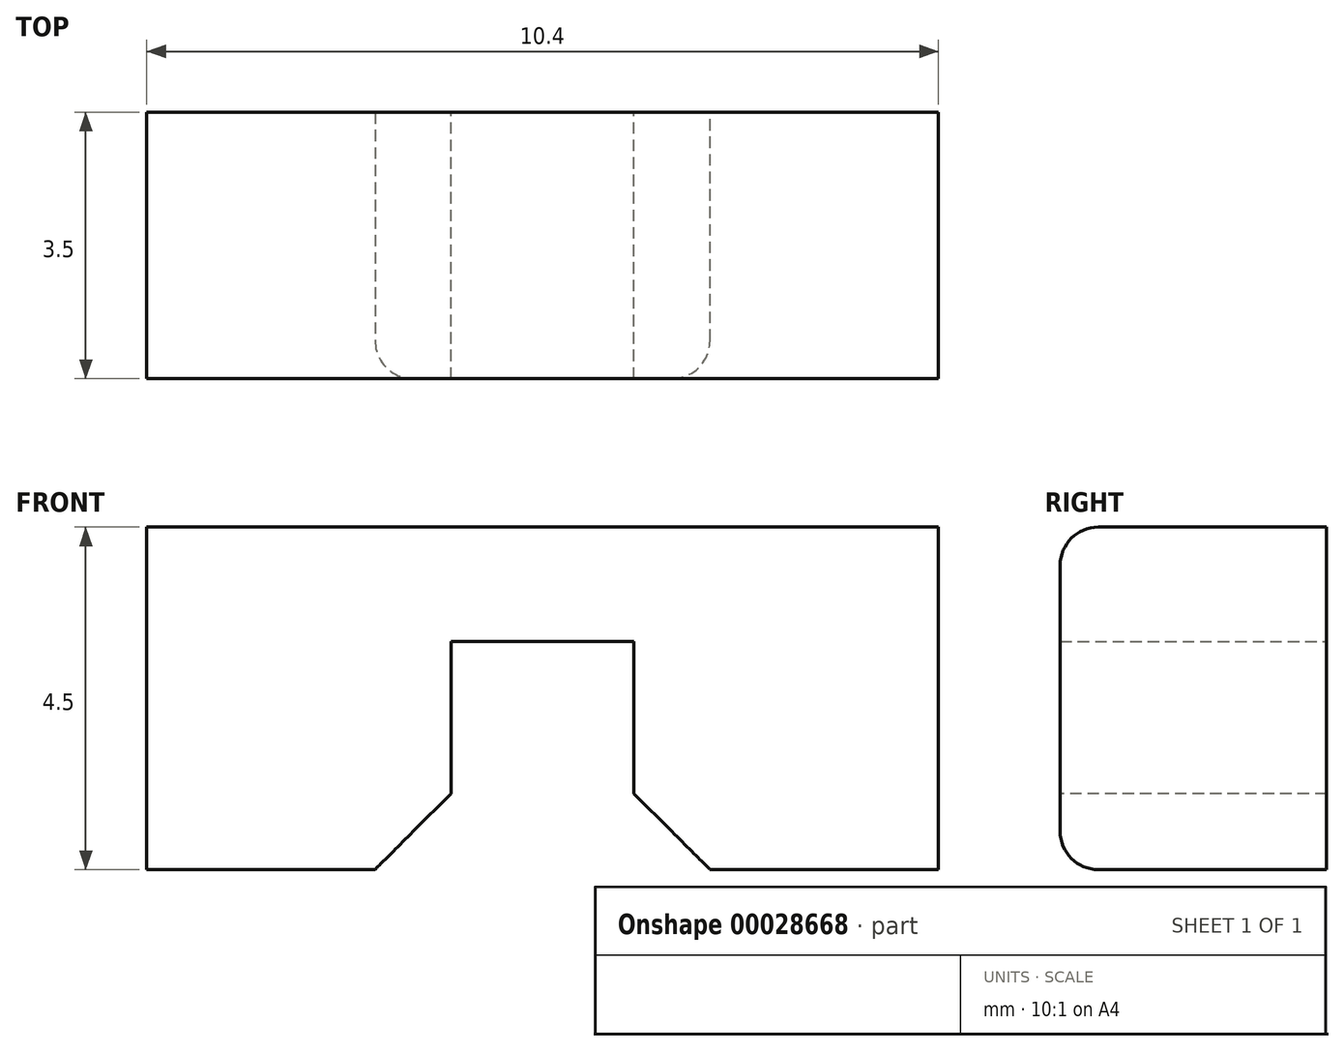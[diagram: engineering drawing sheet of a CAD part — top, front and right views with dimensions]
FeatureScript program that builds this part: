
annotation { "Feature Type Name" : "Feature", "Feature Type Description" : "" }
export const myFeature = defineFeature(function(context is Context, id is Id, definition is map)
    precondition{}
    {
        {
            var Q0;
            Q0=qCreatedBy(makeId("Front.planeOp"),FACE);
            var sketch = newSketch(context, id + "F0", { "sketchPlane" : qUnion([Q0])});
            skLineSegment(sketch, "E0", {"start": v(0, 3) * mm, "end": v(-1.2, 3) * mm});
            skLineSegment(sketch, "E1", {"start": v(-1.2, 3) * mm, "end": v(-1.2, 0) * mm});
            skLineSegment(sketch, "E2", {"start": v(-1.2, 0) * mm, "end": v(-5.2, 0) * mm});
            skLineSegment(sketch, "E3", {"start": v(-5.2, 0) * mm, "end": v(-5.2, 4.5) * mm});
            skLineSegment(sketch, "E4", {"start": v(-5.2, 4.5) * mm, "end": v(0, 4.5) * mm});
            skLineSegment(sketch, "E5.MirrorCS", {"start": v(0, 3) * mm, "end": v(1.2, 3) * mm});
            skLineSegment(sketch, "E6.MirrorCS", {"start": v(1.2, 3) * mm, "end": v(1.2, 0) * mm});
            skLineSegment(sketch, "E7.MirrorCS", {"start": v(1.2, 0) * mm, "end": v(5.2, 0) * mm});
            skLineSegment(sketch, "E8.MirrorCS", {"start": v(5.2, 0) * mm, "end": v(5.2, 4.5) * mm});
            skLineSegment(sketch, "E9.MirrorCS", {"start": v(5.2, 4.5) * mm, "end": v(0, 4.5) * mm});
            skSolve(sketch);
        }
        {
            var Q0;
            Q0 = qSketchRegion(id + "F0", true);
            extrude(context, id + "F1", {"entities" : qUnion([Q0]), "depth" : 3.5 * mm, "offsetDistance" : 25 * mm});
        }
        {
            var Q0;
            Q0=makeQuery(id+"F1.opExtrude","SWEPT_EDGE",EDGE,{"disambiguationData":[OSD([sQuery(id+"F0.wireOp",EDGE,"E1"),sQuery(id+"F0.wireOp",EDGE,"E2")])]});
            var Q1;
            Q1=makeQuery(id+"F1.opExtrude","SWEPT_EDGE",EDGE,{"disambiguationData":[OSD([sQuery(id+"F0.wireOp",EDGE,"E6.MirrorCS"),sQuery(id+"F0.wireOp",EDGE,"E7.MirrorCS")])]});
            chamfer(context, id + "F2", {"entities" : qUnion([Q0, Q1]), "width" : 1 * mm, "tangentPropagation" : true});
        }
        {
            var Q0;
            Q0=makeQuery(id+"F1.opExtrude","CAP_EDGE",EDGE,{"disambiguationData":[OSD([sQuery(id+"F0.wireOp",EDGE,"E4"),sQuery(id+"F0.wireOp",EDGE,"E9.MirrorCS")])],"isStart":false});
            var Q1;
            Q1=makeQuery(id+"F1.opExtrude","CAP_EDGE",EDGE,{"disambiguationData":[OSD([sQuery(id+"F0.wireOp",EDGE,"E2")])],"isStart":false});
            var Q2;
            Q2=makeQuery(id+"F1.opExtrude","CAP_EDGE",EDGE,{"disambiguationData":[OSD([sQuery(id+"F0.wireOp",EDGE,"E7.MirrorCS")])],"isStart":false});
            fillet(context, id + "F3", {"entities" : qUnion([Q0, Q1, Q2]), "radius" : 0.5 * mm, "tangentPropagation" : true, "allowEdgeOverflow" : false});
        }
    });
